# Revit family: P190780JX-052c_JDTSS244GL_Dish_Dishwashers
name_source: partatom
category: Specialty Equipment
units: mm (PartAtom-declared; Revit-internal decimal feet)

## family parameters
Always vertical = Yes
Cut with Voids When Loaded = No
Enable Cutting in Views = No
Maintain Annotation Orientation = No
Part Type = Normal
Room Calculation Point = No
Round Connector Dimension = Use Diameter
Shared = No
Work Plane-Based = No

## types (1)
- JDTSS244GL
    Accent Material = ARCAT - Metal - Steel - Stainless
    Amps = 0 A
    Body Material = ARCAT - Plastic, ABS - Black
    Clearance Material = ARCAT - Clearance
    Default Elevation = 0"
    Depth = 26 1/2"
    Description = RISE™ 24" TriFecta™ Dishwasher, 38 dBA
Lave-vaisselle TriFecta™  RISE™, 38 dBA, 24 po
    Dimension Guide = http://access.whirlpool.com Guide&sku=JDTSS244GL&language=EN
    Door Material = ARCAT - Metal - Steel - Stainless
    Energy Guide = http://access.whirlpool.com Guide&sku=JDTSS244GL&language=EN
    Family Name = DISHWASHERS RISE
    Feature 1 = 38 dBA Tranquility
Tranquillité de 38 dBA
    Feature 2 = TriFecta™ Wash System
Système de lavage TriFecta™
    Feature 3 = Remote Access
Accès à distance
    Handle Material = ARCAT - Metal - Steel - Gray
    Height = 34 1/2"
    Installation-Fabrication = http://access.whirlpool.com Instruction&sku=JDTSS244GL&language=EN
    Manufacturer = Jenn Air
    Model = JDTSS244GL
    Voltage = 0 V
    Width = 23 7/8"

## geometry (parser evidence)
native form markers: Sweep x4
no freeform markers — native parametric forms only
